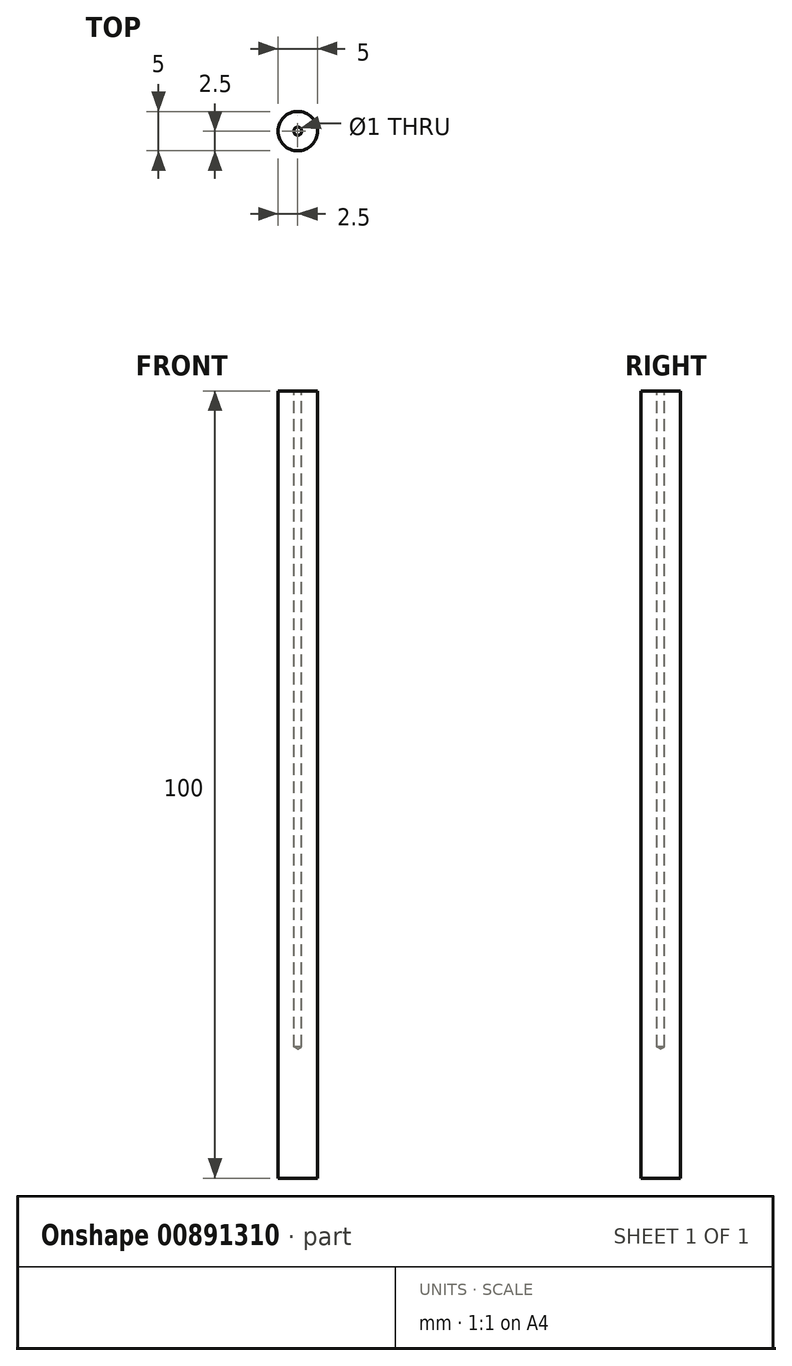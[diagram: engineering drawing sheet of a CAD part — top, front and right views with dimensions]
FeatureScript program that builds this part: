
annotation { "Feature Type Name" : "Feature", "Feature Type Description" : "" }
export const myFeature = defineFeature(function(context is Context, id is Id, definition is map)
    precondition{}
    {
        {
            var Q0;
            Q0=qCreatedBy(makeId("Top.planeOp"),FACE);
            var sketch = newSketch(context, id + "F0", { "sketchPlane" : qUnion([Q0])});
            skCircle(sketch, "E0", {"center": v(0, 0) * mm, "radius": 2.5 * mm});
            skSolve(sketch);
        }
        {
            var Q0;
            Q0=makeQuery(id+"F0.imprint","IMPRINT",FACE,{"disambiguationData":[TD([[makeQuery(id+"F0.imprint","IMPRINT",EDGE,{"derivedFrom":sQuery(id+"F0.wireOp",EDGE,"E0")}),1.0]])]});
            extrude(context, id + "F1", {"entities" : qUnion([Q0]), "depth" : 100 * mm, "offsetDistance" : 25 * mm});
        }
        {
            var Q0;
            Q0=makeQuery(id+"F1.opExtrude","CAP_FACE",FACE,{"disambiguationData":[OSD([sQuery(id+"F0.wireOp",EDGE,"E0")])],"isStart":false});
            var sketch = newSketch(context, id + "F2", { "sketchPlane" : qUnion([Q0])});
            skPoint(sketch, "E1", {"position": v(0, 0) * mm});
            skSolve(sketch);
        }
        {
            var Q0;
            Q0=sQuery(id+"F2.wireOp",VERTEX,"E1");
            var Q1;
            Q1=makeQuery(id+"F1.opExtrude","SWEPT_BODY",BODY,{"disambiguationData":[OSD([sQuery(id+"F0.wireOp",EDGE,"E0")])]});
            hole(context, id + "F3", {"style" : HoleStyle.SIMPLE, "endStyle" : HoleEndStyle.BLIND, "holeDiameter" : 1 * mm, "majorDiameter" : 5 * mm, "holeDepth" : 83.3 * mm, "isTappedThrough" : true, "tappedDepth" : 12 * mm, "tapClearance" : 3, "locations" : qUnion([Q0]), "scope" : qUnion([Q1])});
        }
    });
